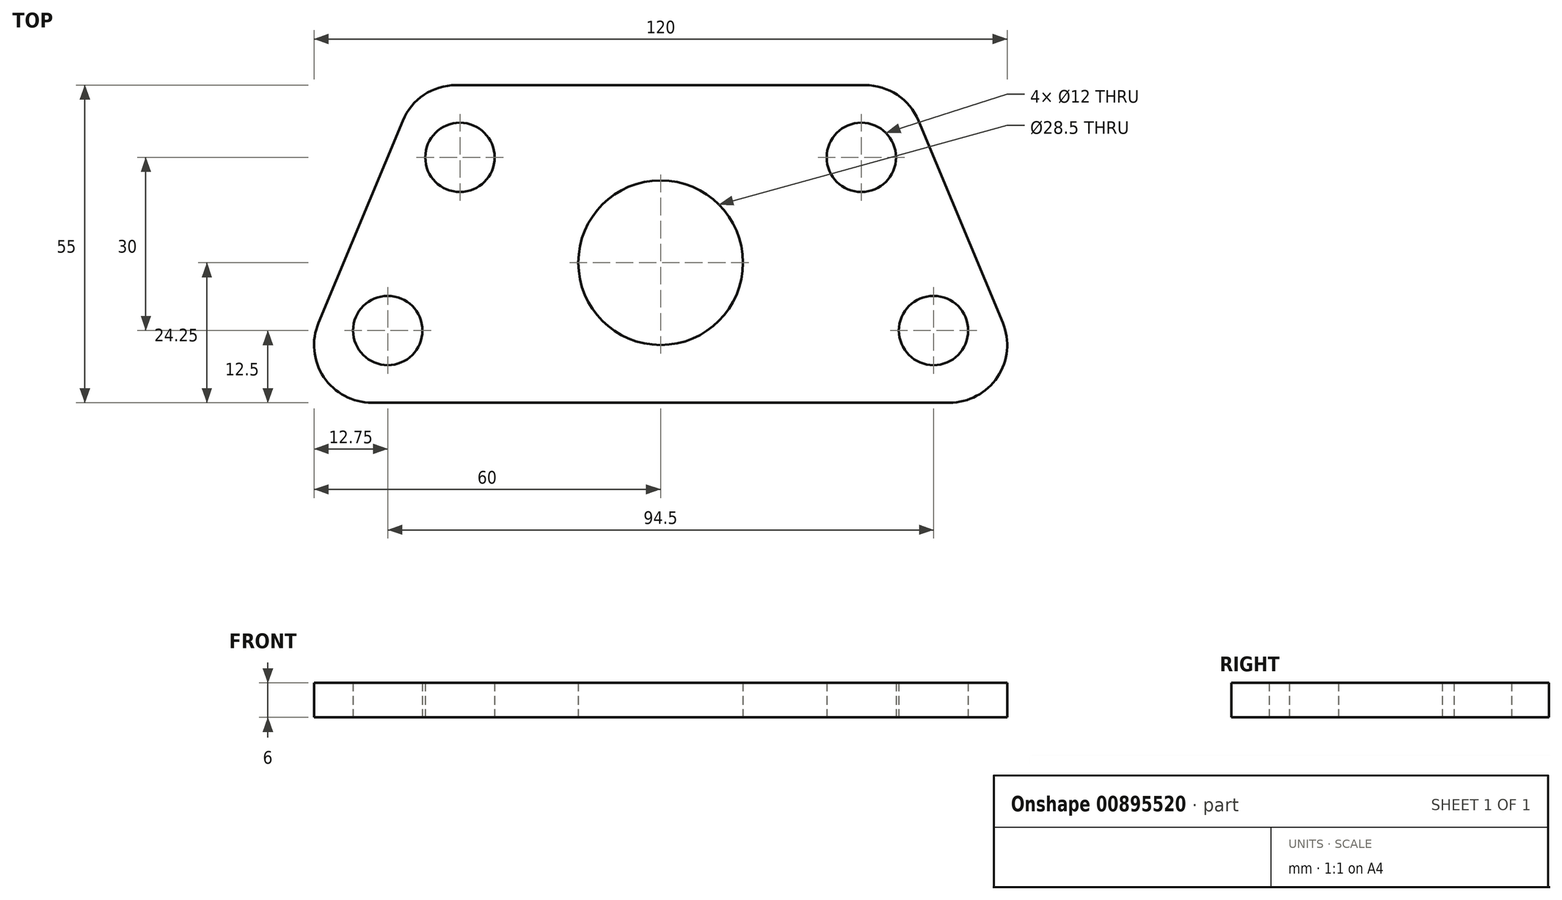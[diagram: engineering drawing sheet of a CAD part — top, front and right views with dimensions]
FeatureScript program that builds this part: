
annotation { "Feature Type Name" : "Feature", "Feature Type Description" : "" }
export const myFeature = defineFeature(function(context is Context, id is Id, definition is map)
    precondition{}
    {
        {
            var Q0;
            Q0=qCreatedBy(makeId("Top.planeOp"),FACE);
            var sketch = newSketch(context, id + "F0", { "sketchPlane" : qUnion([Q0])});
            skLineSegment(sketch, "E0", {"start": v(0, 0) * mm, "end": v(0, -55) * mm, "construction": true});
            skLineSegment(sketch, "E1", {"start": v(0, 0) * mm, "end": v(-35.42, 0) * mm});
            skLineSegment(sketch, "E2", {"start": v(-44.65, -6.15) * mm, "end": v(-59.23, -41.15) * mm});
            skLineSegment(sketch, "E3", {"start": v(-50, -55) * mm, "end": v(0, -55) * mm});
            skCircle(sketch, "E4", {"center": v(-34.75, -12.5) * mm, "radius": 6 * mm});
            skCircle(sketch, "E5", {"center": v(-47.25, -42.5) * mm, "radius": 6 * mm});
            skLineSegment(sketch, "E6", {"start": v(0, -27.5) * mm, "end": v(87.2, -27.5) * mm, "construction": true});
            skLineSegment(sketch, "E7", {"start": v(-34.75, -12.5) * mm, "end": v(-47.25, -42.5) * mm, "construction": true});
            skPoint(sketch, "E8.visualSharp", {"position": v(-42.08, 0) * mm});
            skArc(sketch, "E8.filletArc", {"start": v(-35.42, 0) * mm, "mid": v(-40.96, -1.68) * mm, "end": v(-44.65, -6.15) * mm});
            skPoint(sketch, "E9.visualSharp", {"position": v(-65, -55) * mm});
            skArc(sketch, "E9.filletArc", {"start": v(-59.23, -41.15) * mm, "mid": v(-58.32, -50.55) * mm, "end": v(-50, -55) * mm});
            skLineSegment(sketch, "E10", {"start": v(0, 0) * mm, "end": v(0, -27.5) * mm});
            skArc(sketch, "E11", {"start": v(0, -16.5) * mm, "mid": v(-14.25, -30.75) * mm, "end": v(0, -45) * mm});
            skLineSegment(sketch, "E12.trimOffspring", {"start": v(0, -30.75) * mm, "end": v(0, -55) * mm});
            skSolve(sketch);
        }
        {
            var Q0;
            {var subQ1=sQuery(id+"F0.wireOp",EDGE,"E1");Q0=makeQuery(id+"F0.imprint","IMPRINT",FACE,{"disambiguationData":[TD([[makeQuery(id+"F0.imprint","IMPRINT",EDGE,{"derivedFrom":subQ1}),1.0]])]});}
            extrude(context, id + "F1", {"entities" : qUnion([Q0]), "depth" : 6 * mm, "offsetDistance" : 25 * mm});
        }
        {
            var Q0;
            Q0=makeQuery(id+"F1.opExtrude","SWEPT_BODY",BODY,{"disambiguationData":[OSD([sQuery(id+"F0.wireOp",EDGE,"E1"),sQuery(id+"F0.wireOp",EDGE,"E2"),sQuery(id+"F0.wireOp",EDGE,"E3"),sQuery(id+"F0.wireOp",EDGE,"E4"),sQuery(id+"F0.wireOp",EDGE,"E5"),sQuery(id+"F0.wireOp",EDGE,"E8.filletArc"),sQuery(id+"F0.wireOp",EDGE,"E9.filletArc"),sQuery(id+"F0.wireOp",EDGE,"E10"),sQuery(id+"F0.wireOp",EDGE,"E11"),sQuery(id+"F0.wireOp",EDGE,"E12.trimOffspring")])]});
            var Q1;
            Q1=qCreatedBy(makeId("Right.planeOp"),FACE);
            mirror(context, id + "F2", {"operationType" : NewBodyOperationType.ADD, "entities" : qUnion([Q0]), "mirrorPlane" : qUnion([Q1])});
        }
    });
